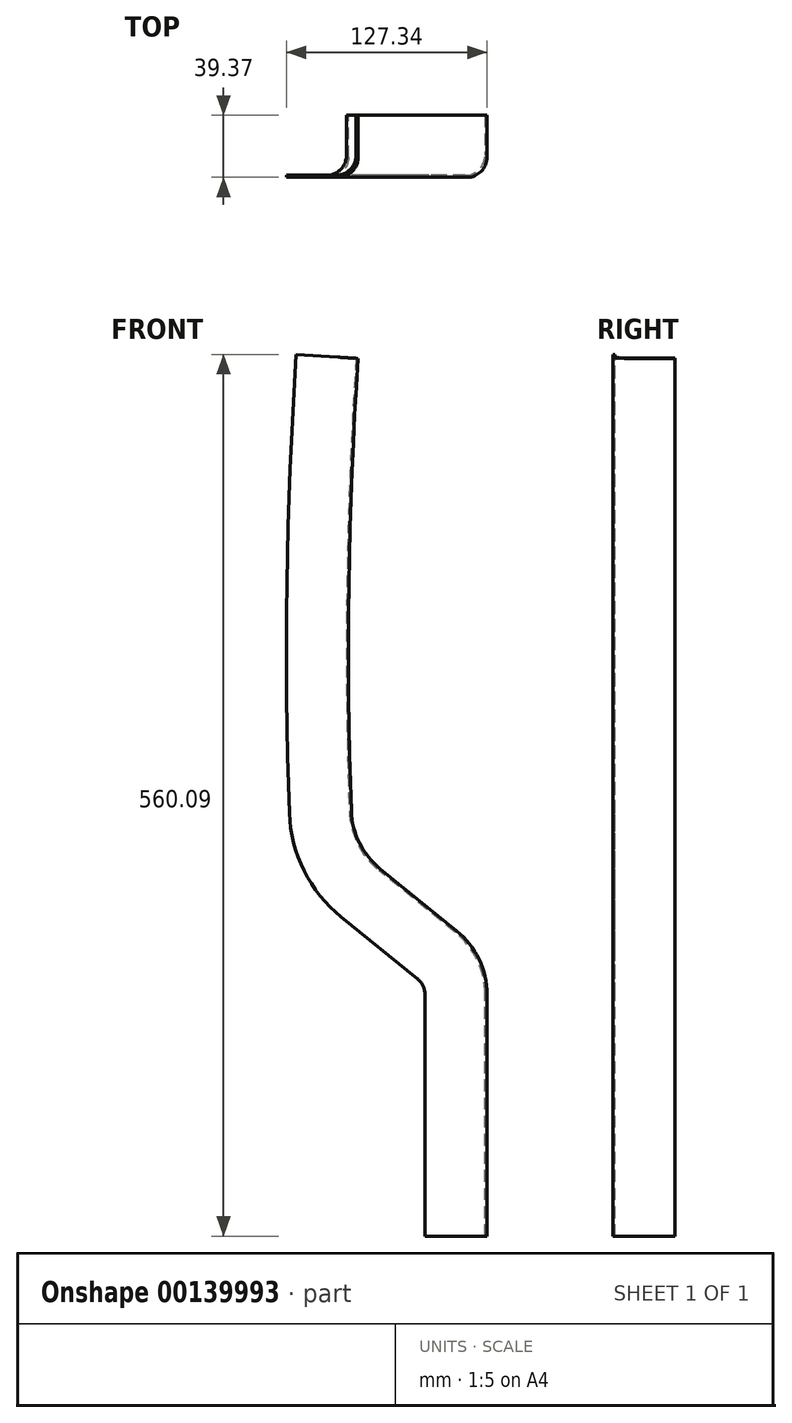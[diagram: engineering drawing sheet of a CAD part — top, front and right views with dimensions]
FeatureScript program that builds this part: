
annotation { "Feature Type Name" : "Feature", "Feature Type Description" : "" }
export const myFeature = defineFeature(function(context is Context, id is Id, definition is map)
    precondition{}
    {
        {
            var Q0;
            Q0=qCreatedBy(makeId("Front.planeOp"),FACE);
            var sketch = newSketch(context, id + "F0", { "sketchPlane" : qUnion([Q0])});
            skLineSegment(sketch, "E0", {"start": v(0, 0) * mm, "end": v(0, 153.57) * mm});
            skLineSegment(sketch, "E1", {"start": v(-18.83, 193.05) * mm, "end": v(-67.39, 232.37) * mm});
            skPoint(sketch, "E2.visualSharp", {"position": v(0, 177.8) * mm});
            skArc(sketch, "E2.filletArc", {"start": v(0, 153.57) * mm, "mid": v(-4.95, 175.44) * mm, "end": v(-18.83, 193.05) * mm});
            skLineSegment(sketch, "E3", {"start": v(0, 275.49) * mm, "end": v(-0.96, 275.49) * mm});
            skLineSegment(sketch, "E4", {"start": v(0, 153.57) * mm, "end": v(0, 154.37) * mm});
            skPoint(sketch, "E4.endSnap0", {"position": v(-4.95, 175.44) * mm});
            skLineSegment(sketch, "E5", {"start": v(-43.64, 799) * mm, "end": v(-81.87, 557.6) * mm});
            skLineSegment(sketch, "E6", {"start": v(63.87, 413.6) * mm, "end": v(391.77, 413.6) * mm, "construction": true});
            skArc(sketch, "E7", {"start": v(-86.19, 270.06) * mm, "mid": v(-80.88, 249.17) * mm, "end": v(-67.39, 232.37) * mm});
            skArc(sketch, "E8", {"start": v(-81.87, 557.6) * mm, "mid": v(-87.65, 413.89) * mm, "end": v(-86.19, 270.06) * mm});
            skPoint(sketch, "E9.orphan", {"position": v(-98.7, 257.72) * mm});
            skArc(sketch, "E10.trimOffspring", {"start": v(-21.32, 223.05) * mm, "mid": v(-21.12, 223.1) * mm, "end": v(-20.9, 223.17) * mm});
            skSolve(sketch);
        }
        {
            var Q0;
            Q0=qCreatedBy(makeId("Top.planeOp"),FACE);
            var sketch = newSketch(context, id + "F1", { "sketchPlane" : qUnion([Q0])});
            skLineSegment(sketch, "E11", {"start": v(0, 0) * mm, "end": v(0, -25.4) * mm});
            skLineSegment(sketch, "E12", {"start": v(1.27, -26.67) * mm, "end": v(1.27, 0) * mm});
            skLineSegment(sketch, "E13", {"start": v(-12.7, -38.1) * mm, "end": v(-38.1, -38.1) * mm});
            skLineSegment(sketch, "E14", {"start": v(-38.1, -38.1) * mm, "end": v(-38.1, -39.37) * mm});
            skLineSegment(sketch, "E15", {"start": v(-38.1, -39.37) * mm, "end": v(-11.43, -39.37) * mm});
            skLineSegment(sketch, "E16", {"start": v(1.27, 0) * mm, "end": v(0, 0) * mm});
            skArc(sketch, "E17.filletArc", {"start": v(-12.7, -38.1) * mm, "mid": v(-3.72, -34.38) * mm, "end": v(0, -25.4) * mm});
            skArc(sketch, "E18.filletArc", {"start": v(-11.43, -39.37) * mm, "mid": v(-2.45, -35.65) * mm, "end": v(1.27, -26.67) * mm});
            skSolve(sketch);
        }
        {
            var Q0;
            Q0=makeQuery(id+"F1.imprint","IMPRINT",FACE,{"disambiguationData":[TD([[makeQuery(id+"F1.imprint","IMPRINT",EDGE,{"derivedFrom":sQuery(id+"F1.wireOp",EDGE,"E11")}),1.0]])]});
            var Q1;
            Q1=sQuery(id+"F0.wireOp",EDGE,"E0");
            var Q2;
            Q2=sQuery(id+"F0.wireOp",EDGE,"E2.filletArc");
            var Q3;
            Q3=sQuery(id+"F0.wireOp",EDGE,"E1");
            var Q4;
            Q4=sQuery(id+"F0.wireOp",EDGE,"E7");
            var Q5;
            Q5=sQuery(id+"F0.wireOp",EDGE,"E8");
            sweep(context, id + "F2", {"profiles" : qUnion([Q0]), "path" : qUnion([Q1, Q2, Q3, Q4, Q5])});
        }
    });
